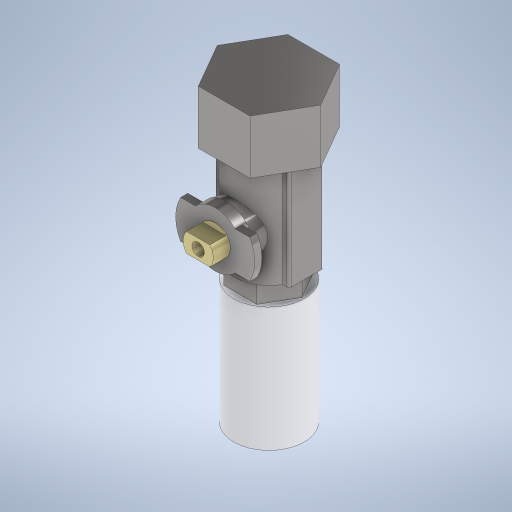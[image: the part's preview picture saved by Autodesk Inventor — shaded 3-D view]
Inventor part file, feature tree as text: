
AUTODESK INVENTOR PART (.ipt)
format: ipt  version: 2023.1 (Build 271208000, 208)  size: 377,344 bytes
history: native  units: mm
features: sketch x9, extrude x8, other x1, fillet x1, revolve x1, projected_geometry x1
ambient origin geometry x8: Origin, YZ Plane, XZ Plane, XY Plane, X Axis, Y Axis, Z Axis, Center Point
bodies: Body1 (feature_tree)
feature tree (21):
  other  "솔리드1"
  extrude  "돌출1"  Depth=25.0mm
  extrude  "돌출2"  Depth=13.0mm TaperAngle=0.0deg
  extrude  "돌출3"  Depth=17.0mm
  extrude  "돌출4"  Depth=18.0mm
  fillet  "모깎기1"  Radius=8.3mm
  sketch  "스케치5"
  revolve  "회전1"
  extrude  "돌출7"  Depth=25.0mm TaperAngle=0.0deg
  sketch  "스케치9"
  extrude  "돌출8"  Depth=16.0mm
  extrude  "돌출9"  Depth=4.5mm TaperAngle=0.0deg
  extrude  "돌출10"  Depth=17.0mm
  sketch  "스케치11"
  sketch  "스케치1"
  sketch  "스케치2"
  sketch  "스케치3"
  sketch  "스케치4"
  sketch  "스케치8"
  projected_geometry  "투영된 루프1"
  sketch  "스케치10"
